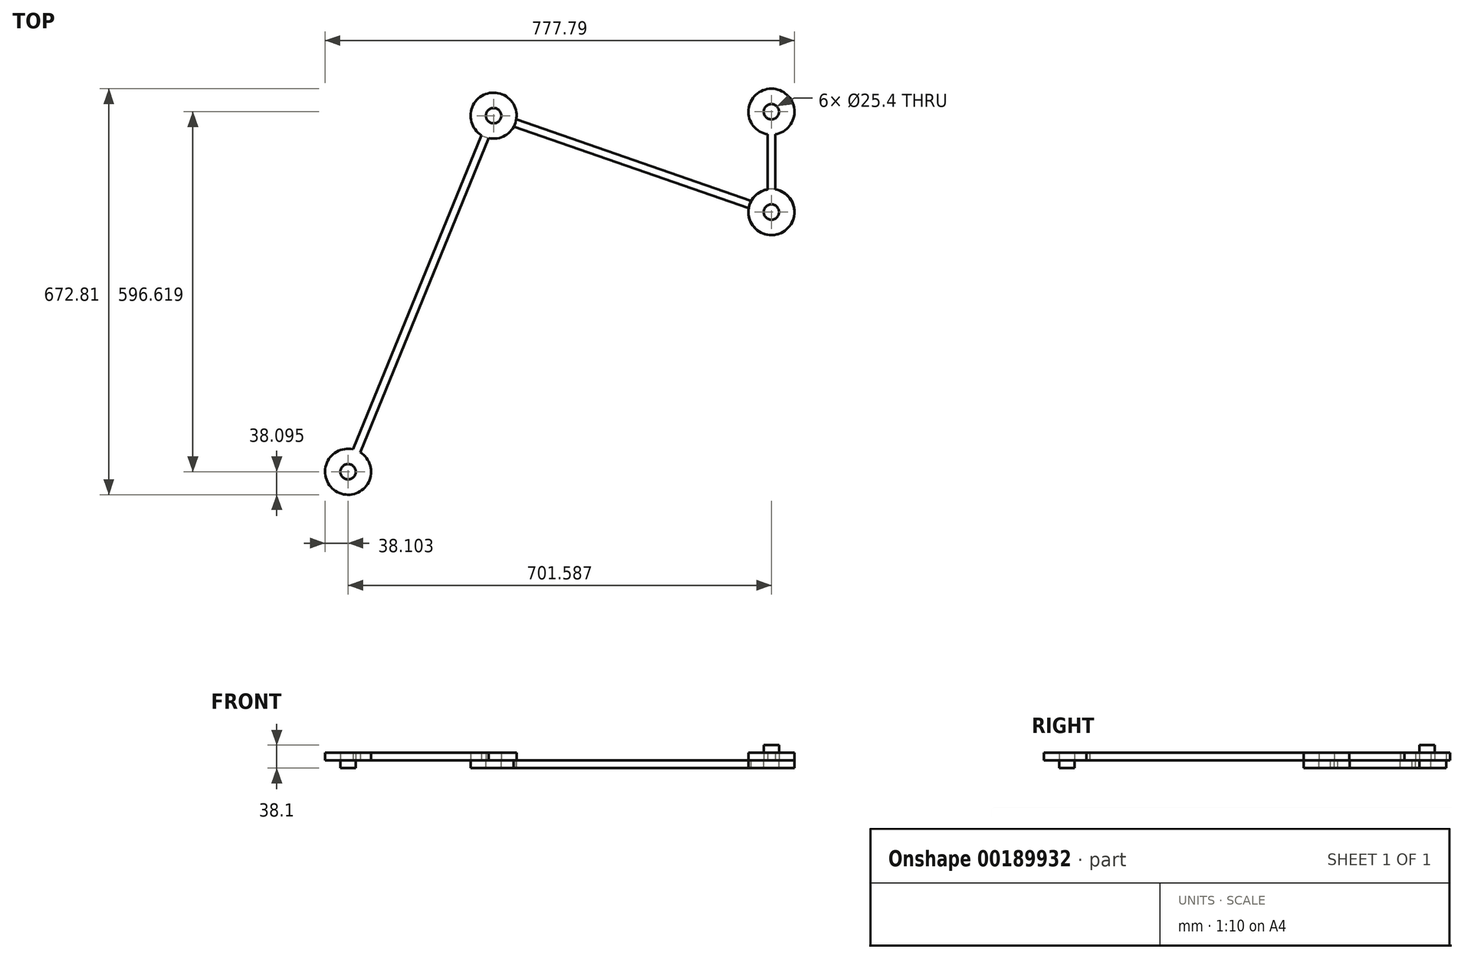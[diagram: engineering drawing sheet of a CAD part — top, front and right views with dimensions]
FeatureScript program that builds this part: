
annotation { "Feature Type Name" : "Feature", "Feature Type Description" : "" }
export const myFeature = defineFeature(function(context is Context, id is Id, definition is map)
    precondition{}
    {
        {
            var Q0;
            Q0=qCreatedBy(makeId("Top.planeOp"),FACE);
            var sketch = newSketch(context, id + "F0", { "sketchPlane" : qUnion([Q0])});
            skCircle(sketch, "E0", {"center": v(0, 0) * mm, "radius": 12.7 * mm});
            skCircle(sketch, "E1", {"center": v(0, 0) * mm, "radius": 38.1 * mm});
            skLineSegment(sketch, "E2.0", {"start": v(-33.41, 18.31) * mm, "end": v(-422.88, 153.42) * mm});
            skLineSegment(sketch, "E3.0", {"start": v(-37.57, 6.31) * mm, "end": v(-427.04, 141.42) * mm});
            skCircle(sketch, "E4", {"center": v(-701.59, -430.36) * mm, "radius": 12.7 * mm});
            skCircle(sketch, "E5", {"center": v(-701.59, -430.36) * mm, "radius": 38.1 * mm});
            skCircle(sketch, "E6", {"center": v(-460.45, 159.73) * mm, "radius": 12.7 * mm});
            skCircle(sketch, "E7", {"center": v(-460.45, 159.73) * mm, "radius": 38.1 * mm});
            skLineSegment(sketch, "E8.0", {"start": v(-480.54, 127.36) * mm, "end": v(-693.25, -393.19) * mm});
            skLineSegment(sketch, "E9.0", {"start": v(-468.78, 122.56) * mm, "end": v(-681.5, -398) * mm});
            skCircle(sketch, "E10", {"center": v(0, 166.25) * mm, "radius": 12.7 * mm});
            skCircle(sketch, "E11", {"center": v(0, 166.25) * mm, "radius": 38.1 * mm});
            skLineSegment(sketch, "E12.0", {"start": v(-6.35, 128.69) * mm, "end": v(-6.35, 37.57) * mm});
            skLineSegment(sketch, "E13.0", {"start": v(6.35, 128.69) * mm, "end": v(6.35, 37.57) * mm});
            skCircle(sketch, "E14", {"center": v(-748.42, -697.52) * mm, "radius": 12.7 * mm});
            skCircle(sketch, "E15", {"center": v(-748.42, -697.52) * mm, "radius": 38.1 * mm});
            skLineSegment(sketch, "E16.0", {"start": v(-735.68, -661.62) * mm, "end": v(-701.82, -468.46) * mm});
            skLineSegment(sketch, "E17.0", {"start": v(-748.19, -659.42) * mm, "end": v(-714.33, -466.27) * mm});
            skLineSegment(sketch, "E18", {"start": v(-718.75, -673.62) * mm, "end": v(-34, -17.18) * mm});
            skPoint(sketch, "E18.startSnap0", {"position": v(-718.75, -565.04) * mm});
            skLineSegment(sketch, "E19", {"start": v(-26.4, -27.47) * mm, "end": v(-712.4, -685.12) * mm});
            skSolve(sketch);
        }
        {
            var Q0;
            Q0=makeQuery(id+"F0.imprint","IMPRINT",FACE,{"disambiguationData":[TD([[makeQuery(id+"F0.imprint","IMPRINT",EDGE,{"derivedFrom":sQuery(id+"F0.wireOp",EDGE,"E10")}),-1.0]])]});
            var Q1;
            {var subQ0=sQuery(id+"F0.wireOp",EDGE,"E12.0");Q1=makeQuery(id+"F0.imprint","IMPRINT",FACE,{"disambiguationData":[TD([[makeQuery(id+"F0.imprint","IMPRINT",EDGE,{"derivedFrom":subQ0}),1.0]])]});}
            var Q2;
            Q2=makeQuery(id+"F0.imprint","IMPRINT",FACE,{"disambiguationData":[TD([[makeQuery(id+"F0.imprint","IMPRINT",EDGE,{"derivedFrom":sQuery(id+"F0.wireOp",EDGE,"E0")}),-1.0]])]});
            extrude(context, id + "F1", {"entities" : qUnion([Q0, Q1, Q2]), "depth" : 12.7 * mm});
        }
        {
            var Q0;
            Q0=makeQuery(id+"F0.imprint","IMPRINT",FACE,{"disambiguationData":[TD([[makeQuery(id+"F0.imprint","IMPRINT",EDGE,{"derivedFrom":sQuery(id+"F0.wireOp",EDGE,"E10")}),1.0]])]});
            extrude(context, id + "F2", {"entities" : qUnion([Q0]), "depth" : 25.4 * mm});
        }
        {
            var Q0;
            Q0=makeQuery(id+"F0.imprint","IMPRINT",FACE,{"disambiguationData":[TD([[makeQuery(id+"F0.imprint","IMPRINT",EDGE,{"derivedFrom":sQuery(id+"F0.wireOp",EDGE,"E6")}),-1.0]])]});
            var Q1;
            {var subQ0=sQuery(id+"F0.wireOp",EDGE,"E2.0");Q1=makeQuery(id+"F0.imprint","IMPRINT",FACE,{"disambiguationData":[TD([[makeQuery(id+"F0.imprint","IMPRINT",EDGE,{"derivedFrom":subQ0}),1.0]])]});}
            var Q2;
            Q2=makeQuery(id+"F0.imprint","IMPRINT",FACE,{"disambiguationData":[TD([[makeQuery(id+"F0.imprint","IMPRINT",EDGE,{"derivedFrom":sQuery(id+"F0.wireOp",EDGE,"E0")}),-1.0]])]});
            extrude(context, id + "F3", {"entities" : qUnion([Q0, Q1, Q2]), "oppositeDirection" : true, "depth" : 12.7 * mm});
        }
        {
            var Q0;
            Q0=makeQuery(id+"F0.imprint","IMPRINT",FACE,{"disambiguationData":[TD([[makeQuery(id+"F0.imprint","IMPRINT",EDGE,{"derivedFrom":sQuery(id+"F0.wireOp",EDGE,"E6")}),-1.0]])]});
            var Q1;
            {var subQ0=sQuery(id+"F0.wireOp",EDGE,"E8.0");Q1=makeQuery(id+"F0.imprint","IMPRINT",FACE,{"disambiguationData":[TD([[makeQuery(id+"F0.imprint","IMPRINT",EDGE,{"derivedFrom":subQ0}),1.0]])]});}
            var Q2;
            Q2=makeQuery(id+"F0.imprint","IMPRINT",FACE,{"disambiguationData":[TD([[makeQuery(id+"F0.imprint","IMPRINT",EDGE,{"derivedFrom":sQuery(id+"F0.wireOp",EDGE,"E4")}),-1.0]])]});
            extrude(context, id + "F4", {"entities" : qUnion([Q0, Q1, Q2]), "depth" : 12.7 * mm});
        }
        {
            var Q0;
            Q0=makeQuery(id+"F0.imprint","IMPRINT",FACE,{"disambiguationData":[TD([[makeQuery(id+"F0.imprint","IMPRINT",EDGE,{"derivedFrom":sQuery(id+"F0.wireOp",EDGE,"E4")}),1.0]])]});
            extrude(context, id + "F5", {"entities" : qUnion([Q0]), "depth" : 12.7 * mm, "hasSecondDirection" : true, "secondDirectionOppositeDirection" : true, "secondDirectionDepth" : 12.7 * mm});
        }
    });
